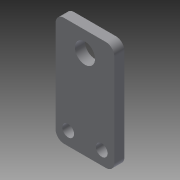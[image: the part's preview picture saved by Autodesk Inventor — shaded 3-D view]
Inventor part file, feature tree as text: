
AUTODESK INVENTOR PART (.ipt)
format: ipt  version: 2015 SP1 (Build 190203100, 203)  size: 102,400 bytes
history: native  units: in
note: dims shown in document units (in); Inventor stores cm internally (conversion verified against a paired STEP export)
features: extrude x1, fillet x1, sketch x1
ambient origin geometry x8: Origin, YZ Plane, XZ Plane, XY Plane, X Axis, Y Axis, Z Axis, Center Point
bodies: Body1 (feature_tree)
feature tree (3):
  extrude  "Extrusion3"  Depth=0.1969in
  fillet  "Fillet2"  Radius=0.2756in
  sketch  "Sketch1"  dims[d3=1.378in d4=0.2756in d6=0.2756in d12=0.4724in d13=0.4724in d22=0.2362in d23=0.0in d24=0.1969in d32=0.7874in d34=1.7717in d35=0.315in]
